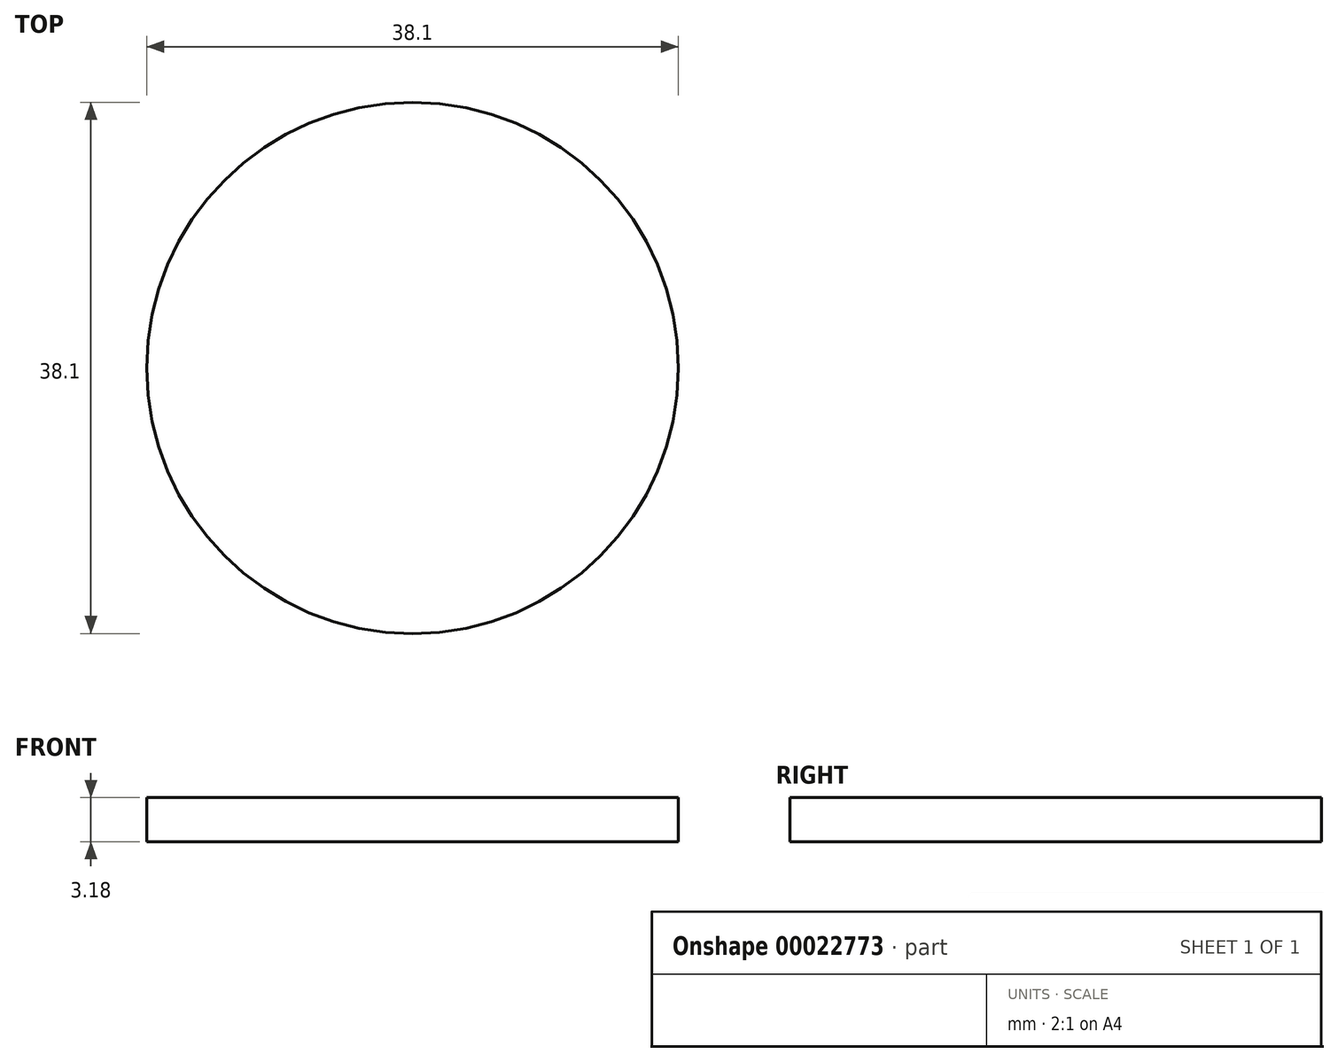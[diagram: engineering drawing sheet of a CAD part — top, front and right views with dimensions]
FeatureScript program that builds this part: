
annotation { "Feature Type Name" : "Feature", "Feature Type Description" : "" }
export const myFeature = defineFeature(function(context is Context, id is Id, definition is map)
    precondition{}
    {
        {
            var Q0;
            Q0=qCreatedBy(makeId("Top.planeOp"),FACE);
            var sketch = newSketch(context, id + "F0", { "sketchPlane" : qUnion([Q0])});
            skCircle(sketch, "E0", {"center": v(0, 0) * mm, "radius": 19.05 * mm});
            skSolve(sketch);
        }
        {
            var Q0;
            Q0=qSketchRegion(id+"F0",true);
            extrude(context, id + "F1", {"entities" : qUnion([Q0]), "depth" : 3.17 * mm});
        }
    });
